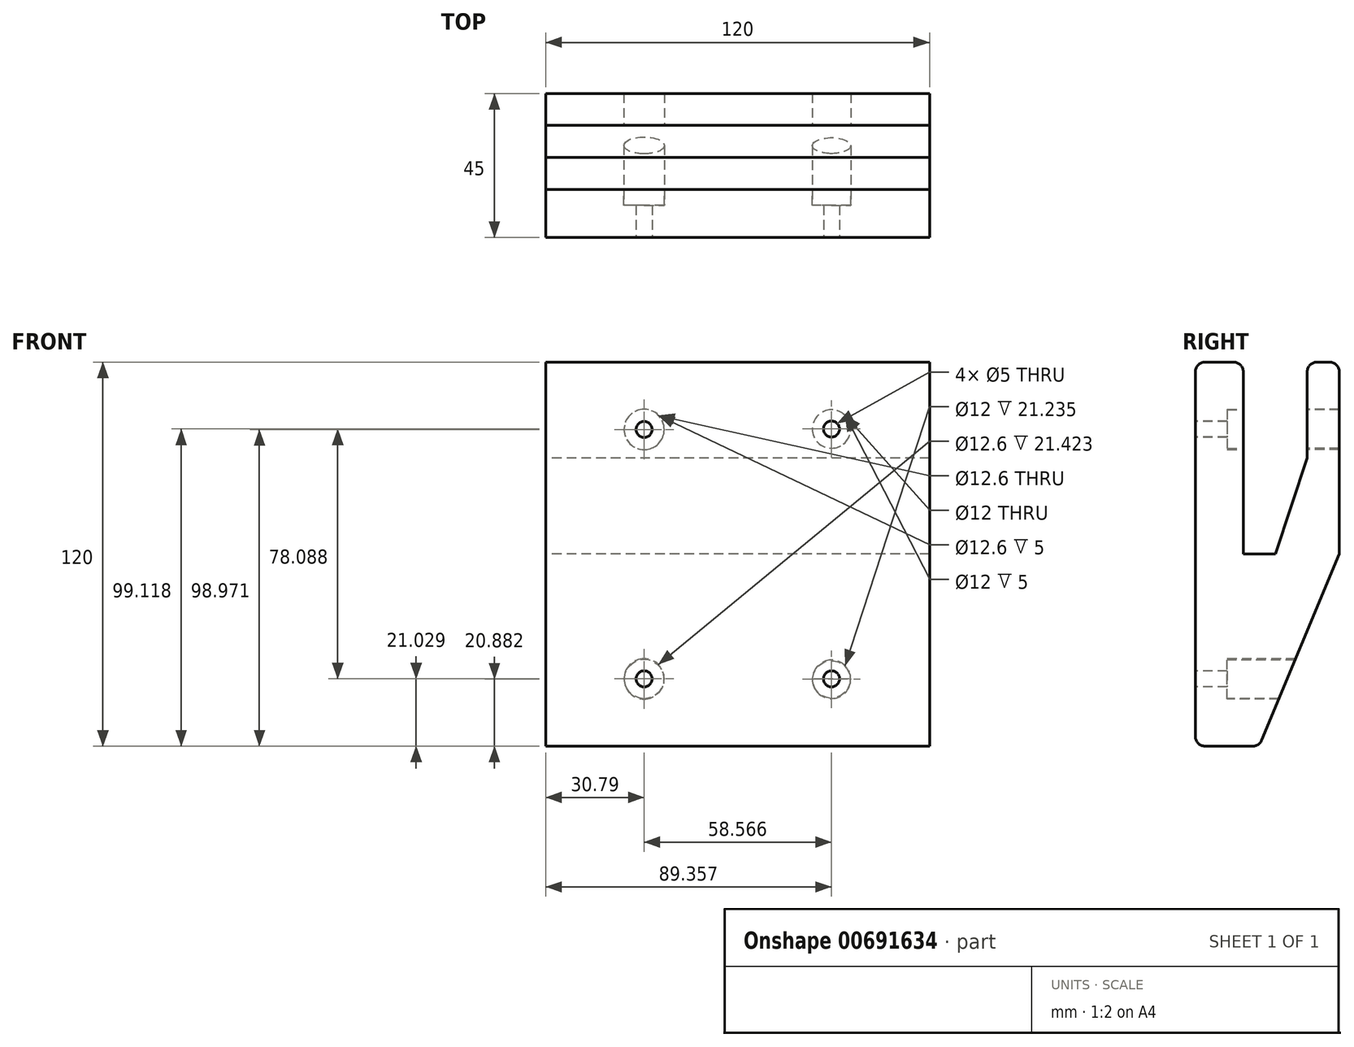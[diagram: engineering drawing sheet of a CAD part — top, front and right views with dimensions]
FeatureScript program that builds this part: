
annotation { "Feature Type Name" : "Feature", "Feature Type Description" : "" }
export const myFeature = defineFeature(function(context is Context, id is Id, definition is map)
    precondition{}
    {
        {
            var Q0;
            Q0=qCreatedBy(makeId("Right.planeOp"),FACE);
            var sketch = newSketch(context, id + "F0", { "sketchPlane" : qUnion([Q0])});
            skLineSegment(sketch, "E0", {"start": v(0, 0) * mm, "end": v(0, 60) * mm});
            skLineSegment(sketch, "E1", {"start": v(0, 0) * mm, "end": v(0, -60) * mm});
            skLineSegment(sketch, "E2", {"start": v(0, 60) * mm, "end": v(15, 60) * mm});
            skLineSegment(sketch, "E3", {"start": v(15, 60) * mm, "end": v(15, 0) * mm});
            skLineSegment(sketch, "E4", {"start": v(15, 0) * mm, "end": v(25, 0) * mm});
            skLineSegment(sketch, "E5", {"start": v(25, 0) * mm, "end": v(35, 30.09) * mm});
            skLineSegment(sketch, "E6", {"start": v(35, 30.09) * mm, "end": v(35, 60) * mm});
            skLineSegment(sketch, "E7", {"start": v(35, 60) * mm, "end": v(45, 60) * mm});
            skLineSegment(sketch, "E8", {"start": v(45, 60) * mm, "end": v(45, 0) * mm});
            skLineSegment(sketch, "E9", {"start": v(45, 0) * mm, "end": v(20, -60) * mm});
            skLineSegment(sketch, "E10", {"start": v(20, -60) * mm, "end": v(0, -60) * mm});
            skSolve(sketch);
        }
        {
            var Q0;
            Q0=makeQuery(id+"F0.imprint","IMPRINT",FACE,{"disambiguationData":[TD([[makeQuery(id+"F0.imprint","IMPRINT",EDGE,{"derivedFrom":sQuery(id+"F0.wireOp",EDGE,"E0")}),-1.0]])]});
            extrude(context, id + "F1", {"entities" : qUnion([Q0]), "depth" : 120 * mm, "offsetDistance" : 25.4 * mm});
        }
        {
            var Q0;
            Q0=makeQuery(id+"F1.opExtrude","SWEPT_FACE",FACE,{"disambiguationData":[OSD([sQuery(id+"F0.wireOp",EDGE,"E0"),sQuery(id+"F0.wireOp",EDGE,"E1")])]});
            var sketch = newSketch(context, id + "F2", { "sketchPlane" : qUnion([Q0])});
            skPoint(sketch, "E11", {"position": v(30.8, 38.97) * mm});
            skPoint(sketch, "E12.MirrorP", {"position": v(30.8, -38.97) * mm});
            skPoint(sketch, "E13.MirrorP", {"position": v(89.36, 39.12) * mm});
            skPoint(sketch, "E14.MirrorP", {"position": v(89.36, -38.97) * mm});
            skCircle(sketch, "E15", {"center": v(89.36, 39.12) * mm, "radius": 2.5 * mm});
            skCircle(sketch, "E16", {"center": v(30.8, 38.97) * mm, "radius": 2.5 * mm});
            skCircle(sketch, "E17", {"center": v(30.8, -38.97) * mm, "radius": 2.5 * mm});
            skCircle(sketch, "E18", {"center": v(89.36, -38.97) * mm, "radius": 2.5 * mm});
            skSolve(sketch);
        }
        {
            var Q0;
            Q0 = qSketchRegion(id + "F2", true);
            extrude(context, id + "F3", {"entities" : qUnion([Q0]), "operationType" : NewBodyOperationType.REMOVE, "endBound" : BoundingType.THROUGH_ALL, "oppositeDirection" : true, "depth" : 21.59 * mm, "offsetDistance" : 25.4 * mm});
        }
        {
            var Q0;
            Q0=makeQuery(id+"F1.opExtrude","SWEPT_FACE",FACE,{"disambiguationData":[OSD([sQuery(id+"F0.wireOp",EDGE,"E3")])]});
            var sketch = newSketch(context, id + "F4", { "sketchPlane" : qUnion([Q0])});
            skCircle(sketch, "E19", {"center": v(-89.36, 39.12) * mm, "radius": 6 * mm});
            skCircle(sketch, "E20", {"center": v(-30.8, 38.97) * mm, "radius": 6.3 * mm});
            skCircle(sketch, "E21.MirrorC", {"center": v(-89.36, -39.12) * mm, "radius": 6 * mm});
            skCircle(sketch, "E22.MirrorC", {"center": v(-30.8, -38.97) * mm, "radius": 6.3 * mm});
            skSolve(sketch);
        }
        {
            var Q0;
            Q0 = qSketchRegion(id + "F4", true);
            extrude(context, id + "F5", {"entities" : qUnion([Q0]), "operationType" : NewBodyOperationType.REMOVE, "depth" : 50.55 * mm, "offsetDistance" : 25.4 * mm});
        }
        {
            var Q0;
            Q0 = qSketchRegion(id + "F4", true);
            extrude(context, id + "F6", {"entities" : qUnion([Q0]), "operationType" : NewBodyOperationType.REMOVE, "oppositeDirection" : true, "depth" : 5 * mm, "offsetDistance" : 25.4 * mm});
        }
        {
            var Q0;
            Q0=makeQuery(id+"F1.opExtrude","SWEPT_EDGE",EDGE,{"disambiguationData":[OSD([sQuery(id+"F0.wireOp",EDGE,"E0"),sQuery(id+"F0.wireOp",EDGE,"E2")])]});
            var Q1;
            Q1=makeQuery(id+"F1.opExtrude","SWEPT_EDGE",EDGE,{"disambiguationData":[OSD([sQuery(id+"F0.wireOp",EDGE,"E2"),sQuery(id+"F0.wireOp",EDGE,"E3")])]});
            var Q2;
            Q2=makeQuery(id+"F1.opExtrude","SWEPT_EDGE",EDGE,{"disambiguationData":[OSD([sQuery(id+"F0.wireOp",EDGE,"E6"),sQuery(id+"F0.wireOp",EDGE,"E7")])]});
            var Q3;
            Q3=makeQuery(id+"F1.opExtrude","SWEPT_EDGE",EDGE,{"disambiguationData":[OSD([sQuery(id+"F0.wireOp",EDGE,"E7"),sQuery(id+"F0.wireOp",EDGE,"E8")])]});
            var Q4;
            Q4=makeQuery(id+"F1.opExtrude","SWEPT_EDGE",EDGE,{"disambiguationData":[OSD([sQuery(id+"F0.wireOp",EDGE,"E1"),sQuery(id+"F0.wireOp",EDGE,"E10")])]});
            var Q5;
            Q5=makeQuery(id+"F1.opExtrude","SWEPT_EDGE",EDGE,{"disambiguationData":[OSD([sQuery(id+"F0.wireOp",EDGE,"E9"),sQuery(id+"F0.wireOp",EDGE,"E10")])]});
            fillet(context, id + "F7", {"entities" : qUnion([Q0, Q1, Q2, Q3, Q4, Q5]), "radius" : 3 * mm, "tangentPropagation" : true, "allowEdgeOverflow" : false});
        }
    });
